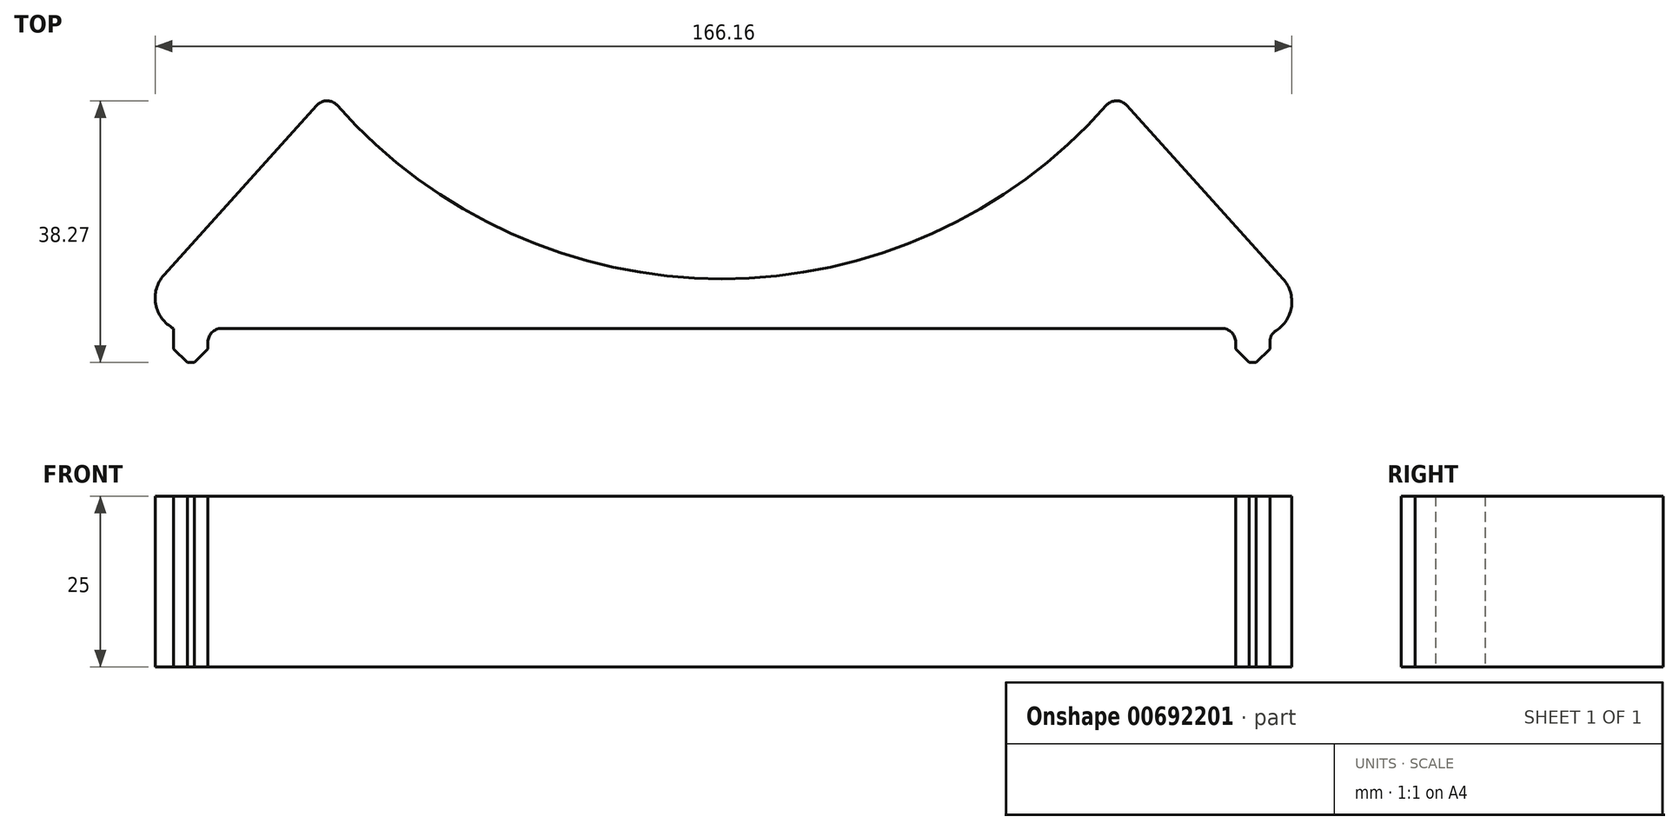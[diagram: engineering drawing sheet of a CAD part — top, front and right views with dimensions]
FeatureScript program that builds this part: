
annotation { "Feature Type Name" : "Feature", "Feature Type Description" : "" }
export const myFeature = defineFeature(function(context is Context, id is Id, definition is map)
    precondition{}
    {
        {
            var Q0;
            Q0=qCreatedBy(makeId("Top.planeOp"),FACE);
            var sketch = newSketch(context, id + "F0", { "sketchPlane" : qUnion([Q0])});
            skArc(sketch, "E0", {"start": v(-57.67, -47.95) * mm, "mid": v(0, -75) * mm, "end": v(57.67, -47.95) * mm});
            skLineSegment(sketch, "E1", {"start": v(88.56, -82.25) * mm, "end": v(0, -82.25) * mm});
            skLineSegment(sketch, "E2", {"start": v(88.56, -82.25) * mm, "end": v(57.67, -47.95) * mm});
            skLineSegment(sketch, "E3.MirrorCS", {"start": v(-88.56, -82.25) * mm, "end": v(-57.67, -47.95) * mm});
            skLineSegment(sketch, "E4.MirrorCS", {"start": v(-88.56, -82.25) * mm, "end": v(0, -82.25) * mm});
            skSolve(sketch);
        }
        {
            var Q0;
            Q0 = qSketchRegion(id + "F0", true);
            extrude(context, id + "F1", {"entities" : qUnion([Q0]), "depth" : 25 * mm, "offsetDistance" : 25 * mm});
        }
        {
            var Q0;
            Q0=makeQuery(id+"F1.opExtrude","SWEPT_FACE",FACE,{"disambiguationData":[OSD([sQuery(id+"F0.wireOp",EDGE,"E1"),sQuery(id+"F0.wireOp",EDGE,"E4.MirrorCS")])]});
            var sketch = newSketch(context, id + "F2", { "sketchPlane" : qUnion([Q0])});
            skLineSegment(sketch, "E5.bottom", {"start": v(75.1, 25) * mm, "end": v(80.1, 25) * mm});
            skLineSegment(sketch, "E5.top", {"start": v(75.1, 0) * mm, "end": v(80.1, 0) * mm});
            skLineSegment(sketch, "E5.left", {"start": v(75.1, 25) * mm, "end": v(75.1, 0) * mm});
            skLineSegment(sketch, "E5.right", {"start": v(80.1, 25) * mm, "end": v(80.1, 0) * mm});
            skLineSegment(sketch, "E6.MirrorCS", {"start": v(-75.1, 25) * mm, "end": v(-75.1, 0) * mm});
            skLineSegment(sketch, "E7.MirrorCS", {"start": v(-75.1, 25) * mm, "end": v(-80.1, 25) * mm});
            skLineSegment(sketch, "E8.MirrorCS", {"start": v(-80.1, 25) * mm, "end": v(-80.1, 0) * mm});
            skLineSegment(sketch, "E9.MirrorCS", {"start": v(-75.1, 0) * mm, "end": v(-80.1, 0) * mm});
            skSolve(sketch);
        }
        {
            var Q0;
            Q0 = qSketchRegion(id + "F2", true);
            extrude(context, id + "F3", {"entities" : qUnion([Q0]), "operationType" : NewBodyOperationType.ADD, "depth" : 5 * mm, "offsetDistance" : 25 * mm});
        }
        {
            var Q0;
            Q0=makeQuery(id+"F3.opExtrude","CAP_EDGE",EDGE,{"disambiguationData":[OSD([sQuery(id+"F2.wireOp",EDGE,"E8.MirrorCS")])],"isStart":false});
            var Q1;
            Q1=makeQuery(id+"F3.opExtrude","CAP_EDGE",EDGE,{"disambiguationData":[OSD([sQuery(id+"F2.wireOp",EDGE,"E6.MirrorCS")])],"isStart":false});
            var Q2;
            Q2=makeQuery(id+"F3.opExtrude","CAP_EDGE",EDGE,{"disambiguationData":[OSD([sQuery(id+"F2.wireOp",EDGE,"E5.left")])],"isStart":false});
            var Q3;
            Q3=makeQuery(id+"F3.opExtrude","CAP_EDGE",EDGE,{"disambiguationData":[OSD([sQuery(id+"F2.wireOp",EDGE,"E5.right")])],"isStart":false});
            chamfer(context, id + "F4", {"entities" : qUnion([Q0, Q1, Q2, Q3]), "width" : 2 * mm, "tangentPropagation" : true});
        }
        {
            var Q0;
            Q0=makeQuery(id+"F3.opExtrude","CAP_EDGE",EDGE,{"disambiguationData":[OSD([sQuery(id+"F2.wireOp",EDGE,"E8.MirrorCS")])],"isStart":true});
            var Q1;
            Q1=makeQuery(id+"F3.opExtrude","CAP_EDGE",EDGE,{"disambiguationData":[OSD([sQuery(id+"F2.wireOp",EDGE,"E6.MirrorCS")])],"isStart":true});
            var Q2;
            Q2=makeQuery(id+"F3.opExtrude","CAP_EDGE",EDGE,{"disambiguationData":[OSD([sQuery(id+"F2.wireOp",EDGE,"E5.right")])],"isStart":true});
            var Q3;
            Q3=makeQuery(id+"F3.opExtrude","CAP_EDGE",EDGE,{"disambiguationData":[OSD([sQuery(id+"F2.wireOp",EDGE,"E5.left")])],"isStart":true});
            var Q4;
            Q4=makeQuery(id+"F1.opExtrude","SWEPT_EDGE",EDGE,{"disambiguationData":[OSD([sQuery(id+"F0.wireOp",EDGE,"E0"),sQuery(id+"F0.wireOp",EDGE,"E2")])]});
            var Q5;
            Q5=makeQuery(id+"F1.opExtrude","SWEPT_EDGE",EDGE,{"disambiguationData":[OSD([sQuery(id+"F0.wireOp",EDGE,"E0"),sQuery(id+"F0.wireOp",EDGE,"E3.MirrorCS")])]});
            fillet(context, id + "F5", {"entities" : qUnion([Q0, Q1, Q2, Q3, Q4, Q5]), "radius" : 2 * mm, "tangentPropagation" : true, "allowEdgeOverflow" : false});
        }
        {
            var Q0;
            Q0=makeQuery(id+"F1.opExtrude","SWEPT_EDGE",EDGE,{"disambiguationData":[OSD([sQuery(id+"F0.wireOp",EDGE,"E3.MirrorCS"),sQuery(id+"F0.wireOp",EDGE,"E4.MirrorCS")])]});
            var Q1;
            Q1=makeQuery(id+"F1.opExtrude","SWEPT_EDGE",EDGE,{"disambiguationData":[OSD([sQuery(id+"F0.wireOp",EDGE,"E1"),sQuery(id+"F0.wireOp",EDGE,"E2")])]});
            fillet(context, id + "F6", {"entities" : qUnion([Q0, Q1]), "radius" : 5 * mm, "tangentPropagation" : true, "allowEdgeOverflow" : false});
        }
    });
